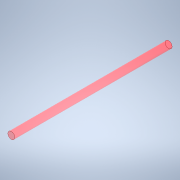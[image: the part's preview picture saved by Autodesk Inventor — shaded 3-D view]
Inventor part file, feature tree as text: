
AUTODESK INVENTOR PART (.ipt)
format: ipt  version: 2020 (Build 240168000, 168)  size: 101,376 bytes
history: native  units: mm
features: other x1, extrude x1, sketch x1
ambient origin geometry x8: Origin, YZ Plane, XZ Plane, XY Plane, X Axis, Y Axis, Z Axis, Center Point
bodies: Body1 (feature_tree)
feature tree (3):
  other  "솔리드1"
  extrude  "돌출1"  Depth=1.0mm
  sketch  "스케치1"
